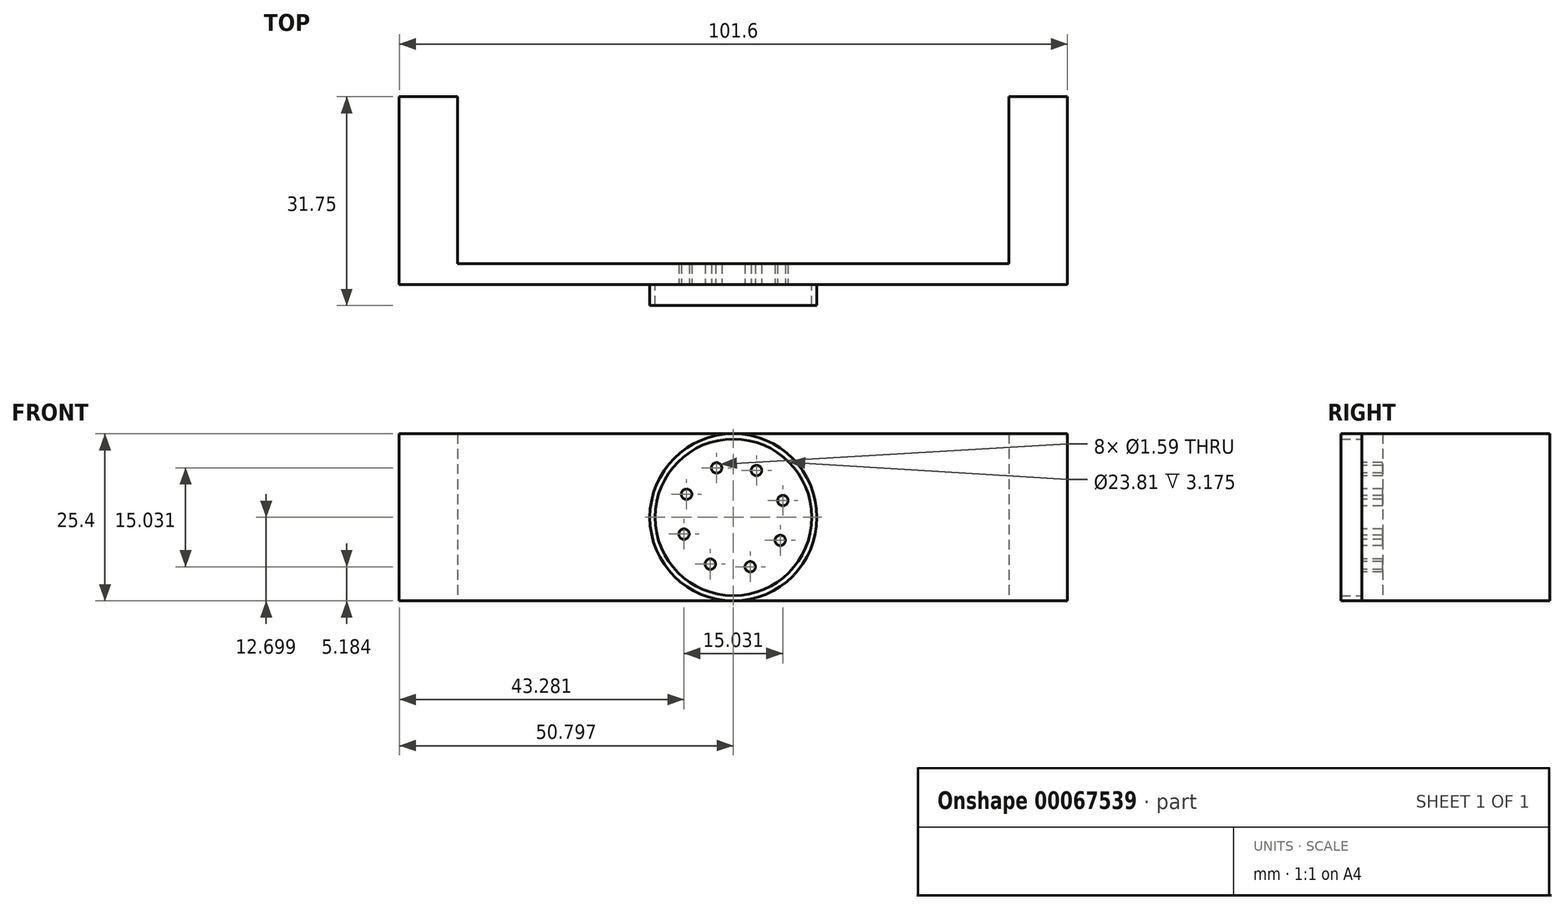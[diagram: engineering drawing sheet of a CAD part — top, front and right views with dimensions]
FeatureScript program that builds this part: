
annotation { "Feature Type Name" : "Feature", "Feature Type Description" : "" }
export const myFeature = defineFeature(function(context is Context, id is Id, definition is map)
    precondition{}
    {
        {
            var Q0;
            Q0=qCreatedBy(makeId("Front.planeOp"),FACE);
            var sketch = newSketch(context, id + "F0", { "sketchPlane" : qUnion([Q0])});
            skLineSegment(sketch, "E0.bottom", {"start": v(14.55, 17.39) * mm, "end": v(116.15, 17.39) * mm});
            skLineSegment(sketch, "E0.top", {"start": v(14.55, -8.01) * mm, "end": v(116.15, -8.01) * mm});
            skLineSegment(sketch, "E0.left", {"start": v(14.55, 17.39) * mm, "end": v(14.55, -8.01) * mm});
            skLineSegment(sketch, "E0.right", {"start": v(116.15, 17.39) * mm, "end": v(116.15, -8.01) * mm});
            skSolve(sketch);
        }
        {
            var Q0;
            Q0=makeQuery(id+"F0.imprint","IMPRINT",FACE,{"disambiguationData":[TD([[makeQuery(id+"F0.imprint","IMPRINT",EDGE,{"derivedFrom":sQuery(id+"F0.wireOp",EDGE,"E0.bottom")}),-1.0]])]});
            extrude(context, id + "F1", {"entities" : qUnion([Q0]), "depth" : 3.17 * mm});
        }
        {
            var Q0;
            Q0=makeQuery(id+"F1.opExtrude","CAP_FACE",FACE,{"disambiguationData":[OSD([sQuery(id+"F0.wireOp",EDGE,"E0.bottom"),sQuery(id+"F0.wireOp",EDGE,"E0.top"),sQuery(id+"F0.wireOp",EDGE,"E0.left"),sQuery(id+"F0.wireOp",EDGE,"E0.right")])],"isStart":true});
            var sketch = newSketch(context, id + "F2", { "sketchPlane" : qUnion([Q0])});
            skLineSegment(sketch, "E1.bottom", {"start": v(-116.15, 17.39) * mm, "end": v(-107.26, 17.39) * mm});
            skLineSegment(sketch, "E1.top", {"start": v(-116.15, -8.01) * mm, "end": v(-107.26, -8.01) * mm});
            skLineSegment(sketch, "E1.left", {"start": v(-116.15, 17.39) * mm, "end": v(-116.15, -8.01) * mm});
            skLineSegment(sketch, "E1.right", {"start": v(-107.26, 17.39) * mm, "end": v(-107.26, -8.01) * mm});
            skLineSegment(sketch, "E2.bottom", {"start": v(-14.55, 17.39) * mm, "end": v(-23.44, 17.39) * mm});
            skLineSegment(sketch, "E2.top", {"start": v(-14.55, -8.01) * mm, "end": v(-23.44, -8.01) * mm});
            skLineSegment(sketch, "E2.left", {"start": v(-14.55, 17.39) * mm, "end": v(-14.55, -8.01) * mm});
            skLineSegment(sketch, "E2.right", {"start": v(-23.44, 17.39) * mm, "end": v(-23.44, -8.01) * mm});
            skSolve(sketch);
        }
        {
            var Q0;
            Q0=makeQuery(id+"F2.imprint","IMPRINT",FACE,{"disambiguationData":[TD([[makeQuery(id+"F2.imprint","IMPRINT",EDGE,{"derivedFrom":sQuery(id+"F2.wireOp",EDGE,"E1.bottom")}),1.0]])]});
            extrude(context, id + "F3", {"entities" : qUnion([Q0]), "operationType" : NewBodyOperationType.ADD, "depth" : 25.4 * mm});
        }
        {
            var Q0;
            Q0=makeQuery(id+"F2.imprint","IMPRINT",FACE,{"disambiguationData":[TD([[makeQuery(id+"F2.imprint","IMPRINT",EDGE,{"derivedFrom":sQuery(id+"F2.wireOp",EDGE,"E2.bottom")}),1.0]])]});
            extrude(context, id + "F4", {"entities" : qUnion([Q0]), "operationType" : NewBodyOperationType.ADD, "depth" : 25.4 * mm});
        }
        {
            var Q0;
            Q0=makeQuery(id+"F1.opExtrude","CAP_FACE",FACE,{"disambiguationData":[OSD([sQuery(id+"F0.wireOp",EDGE,"E0.bottom"),sQuery(id+"F0.wireOp",EDGE,"E0.top"),sQuery(id+"F0.wireOp",EDGE,"E0.left"),sQuery(id+"F0.wireOp",EDGE,"E0.right")])],"isStart":false});
            var sketch = newSketch(context, id + "F5", { "sketchPlane" : qUnion([Q0])});
            skLineSegment(sketch, "E3", {"start": v(65.35, 17.39) * mm, "end": v(65.35, -8.01) * mm, "construction": true});
            skLineSegment(sketch, "E4", {"start": v(14.55, 4.69) * mm, "end": v(116.15, 4.69) * mm, "construction": true});
            skCircle(sketch, "E5", {"center": v(65.35, 4.69) * mm, "radius": 11.9 * mm});
            skCircle(sketch, "E6", {"center": v(65.35, 4.69) * mm, "radius": 12.7 * mm});
            skSolve(sketch);
        }
        {
            var Q0;
            Q0=makeQuery(id+"F5.imprint","IMPRINT",FACE,{"disambiguationData":[TD([[makeQuery(id+"F5.imprint","IMPRINT",EDGE,{"derivedFrom":sQuery(id+"F5.wireOp",EDGE,"E5")}),-1.0]])]});
            extrude(context, id + "F6", {"entities" : qUnion([Q0]), "operationType" : NewBodyOperationType.ADD, "depth" : 3.17 * mm});
        }
        {
            var Q0;
            Q0=makeQuery(id+"F6.boolean.opBoolean","SPLIT",FACE,{"disambiguationData":[TD([makeQuery(id+"F6.opExtrude","SWEPT_FACE",FACE,{"disambiguationData":[OSD([sQuery(id+"F5.wireOp",EDGE,"E5")])]})])],"derivedFrom":makeQuery(id+"F1.opExtrude","CAP_FACE",FACE,{"disambiguationData":[OSD([sQuery(id+"F0.wireOp",EDGE,"E0.bottom"),sQuery(id+"F0.wireOp",EDGE,"E0.top"),sQuery(id+"F0.wireOp",EDGE,"E0.left"),sQuery(id+"F0.wireOp",EDGE,"E0.right")])],"isStart":false})});
            var sketch = newSketch(context, id + "F7", { "sketchPlane" : qUnion([Q0])});
            skCircle(sketch, "E7", {"center": v(65.35, 4.69) * mm, "radius": 7.94 * mm, "construction": true});
            skLineSegment(sketch, "E8", {"start": v(65.35, 4.69) * mm, "end": v(58.23, 8.2) * mm, "construction": true});
            skLineSegment(sketch, "E9", {"start": v(57.83, 2.14) * mm, "end": v(65.35, 4.69) * mm, "construction": true});
            skLineSegment(sketch, "E10", {"start": v(65.35, 4.69) * mm, "end": v(62.8, 12.2) * mm, "construction": true});
            skLineSegment(sketch, "E11", {"start": v(65.35, 4.69) * mm, "end": v(68.85, 11.8) * mm, "construction": true});
            skLineSegment(sketch, "E12", {"start": v(65.35, 4.69) * mm, "end": v(67.9, -2.83) * mm, "construction": true});
            skLineSegment(sketch, "E13", {"start": v(65.35, 4.69) * mm, "end": v(72.47, 1.18) * mm, "construction": true});
            skLineSegment(sketch, "E14", {"start": v(65.35, 4.69) * mm, "end": v(72.86, 7.24) * mm, "construction": true});
            skLineSegment(sketch, "E15", {"start": v(65.35, 4.69) * mm, "end": v(61.84, -2.43) * mm, "construction": true});
            skCircle(sketch, "E16", {"center": v(62.8, 12.2) * mm, "radius": 0.8 * mm});
            skCircle(sketch, "E17", {"center": v(68.85, 11.8) * mm, "radius": 0.8 * mm});
            skCircle(sketch, "E18", {"center": v(72.86, 7.24) * mm, "radius": 0.8 * mm});
            skCircle(sketch, "E19", {"center": v(72.47, 1.18) * mm, "radius": 0.8 * mm});
            skCircle(sketch, "E20", {"center": v(67.9, -2.83) * mm, "radius": 0.8 * mm});
            skCircle(sketch, "E21", {"center": v(61.84, -2.43) * mm, "radius": 0.8 * mm});
            skCircle(sketch, "E22", {"center": v(57.83, 2.14) * mm, "radius": 0.8 * mm});
            skCircle(sketch, "E23", {"center": v(58.23, 8.2) * mm, "radius": 0.8 * mm});
            skSolve(sketch);
        }
        {
            var Q0;
            Q0=makeQuery(id+"F7.imprint","IMPRINT",FACE,{"disambiguationData":[TD([[makeQuery(id+"F7.imprint","IMPRINT",EDGE,{"derivedFrom":sQuery(id+"F7.wireOp",EDGE,"E23")}),1.0]])]});
            var Q1;
            Q1=makeQuery(id+"F7.imprint","IMPRINT",FACE,{"disambiguationData":[TD([[makeQuery(id+"F7.imprint","IMPRINT",EDGE,{"derivedFrom":sQuery(id+"F7.wireOp",EDGE,"E16")}),1.0]])]});
            var Q2;
            Q2=makeQuery(id+"F7.imprint","IMPRINT",FACE,{"disambiguationData":[TD([[makeQuery(id+"F7.imprint","IMPRINT",EDGE,{"derivedFrom":sQuery(id+"F7.wireOp",EDGE,"E17")}),1.0]])]});
            var Q3;
            Q3=makeQuery(id+"F7.imprint","IMPRINT",FACE,{"disambiguationData":[TD([[makeQuery(id+"F7.imprint","IMPRINT",EDGE,{"derivedFrom":sQuery(id+"F7.wireOp",EDGE,"E18")}),1.0]])]});
            var Q4;
            Q4=makeQuery(id+"F7.imprint","IMPRINT",FACE,{"disambiguationData":[TD([[makeQuery(id+"F7.imprint","IMPRINT",EDGE,{"derivedFrom":sQuery(id+"F7.wireOp",EDGE,"E19")}),1.0]])]});
            var Q5;
            Q5=makeQuery(id+"F7.imprint","IMPRINT",FACE,{"disambiguationData":[TD([[makeQuery(id+"F7.imprint","IMPRINT",EDGE,{"derivedFrom":sQuery(id+"F7.wireOp",EDGE,"E20")}),1.0]])]});
            var Q6;
            Q6=makeQuery(id+"F7.imprint","IMPRINT",FACE,{"disambiguationData":[TD([[makeQuery(id+"F7.imprint","IMPRINT",EDGE,{"derivedFrom":sQuery(id+"F7.wireOp",EDGE,"E21")}),1.0]])]});
            var Q7;
            Q7=makeQuery(id+"F7.imprint","IMPRINT",FACE,{"disambiguationData":[TD([[makeQuery(id+"F7.imprint","IMPRINT",EDGE,{"derivedFrom":sQuery(id+"F7.wireOp",EDGE,"E22")}),1.0]])]});
            extrude(context, id + "F8", {"entities" : qUnion([Q0, Q1, Q2, Q3, Q4, Q5, Q6, Q7]), "operationType" : NewBodyOperationType.REMOVE, "oppositeDirection" : true, "depth" : 25.4 * mm});
        }
    });
